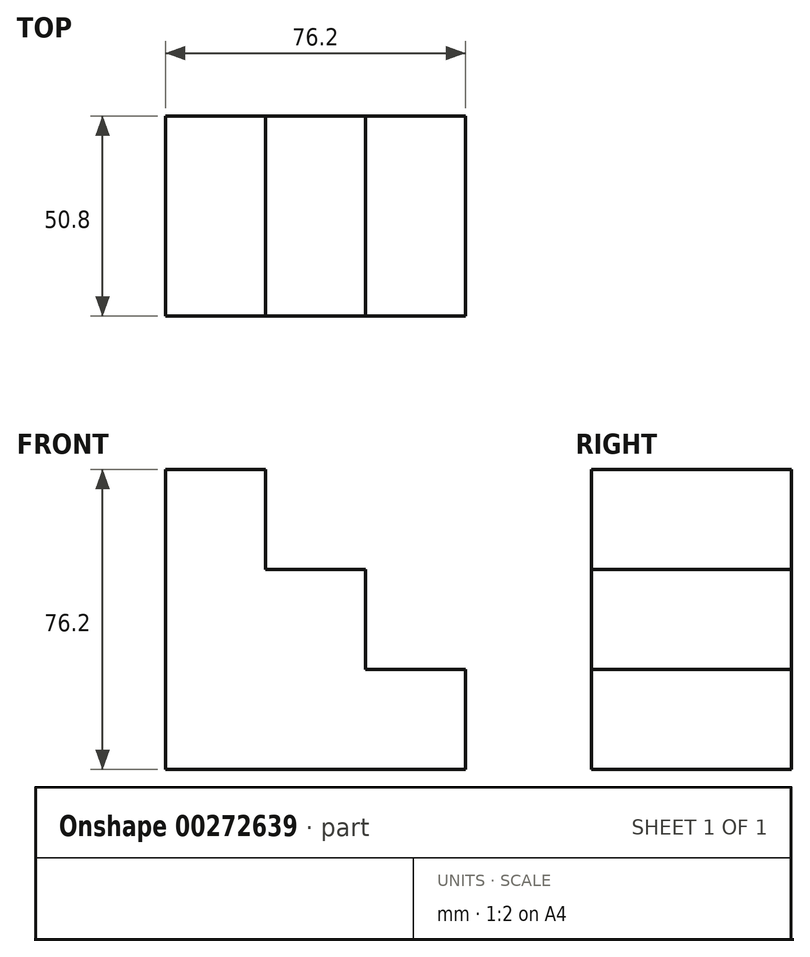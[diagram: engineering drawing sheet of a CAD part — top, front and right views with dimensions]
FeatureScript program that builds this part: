
annotation { "Feature Type Name" : "Feature", "Feature Type Description" : "" }
export const myFeature = defineFeature(function(context is Context, id is Id, definition is map)
    precondition{}
    {
        {
            var Q0;
            Q0=qCreatedBy(makeId("Front.planeOp"),FACE);
            var sketch = newSketch(context, id + "F0", { "sketchPlane" : qUnion([Q0])});
            skLineSegment(sketch, "E0", {"start": v(-38, 42.21) * mm, "end": v(-38, -33.99) * mm});
            skLineSegment(sketch, "E1", {"start": v(-38, -33.99) * mm, "end": v(38.2, -33.99) * mm});
            skLineSegment(sketch, "E2", {"start": v(-38, 42.21) * mm, "end": v(-12.6, 42.21) * mm});
            skLineSegment(sketch, "E3", {"start": v(-12.6, 42.21) * mm, "end": v(-12.6, 16.81) * mm});
            skLineSegment(sketch, "E4", {"start": v(-12.6, 16.81) * mm, "end": v(12.8, 16.81) * mm});
            skLineSegment(sketch, "E5", {"start": v(12.8, 16.81) * mm, "end": v(12.8, -8.59) * mm});
            skLineSegment(sketch, "E6", {"start": v(12.8, -8.59) * mm, "end": v(38.2, -8.59) * mm});
            skLineSegment(sketch, "E7", {"start": v(38.2, -8.59) * mm, "end": v(38.2, -33.99) * mm});
            skSolve(sketch);
        }
        {
            var Q0;
            Q0 = qSketchRegion(id + "F0", true);
            extrude(context, id + "F1", {"entities" : qUnion([Q0]), "depth" : 50.8 * mm});
        }
    });
